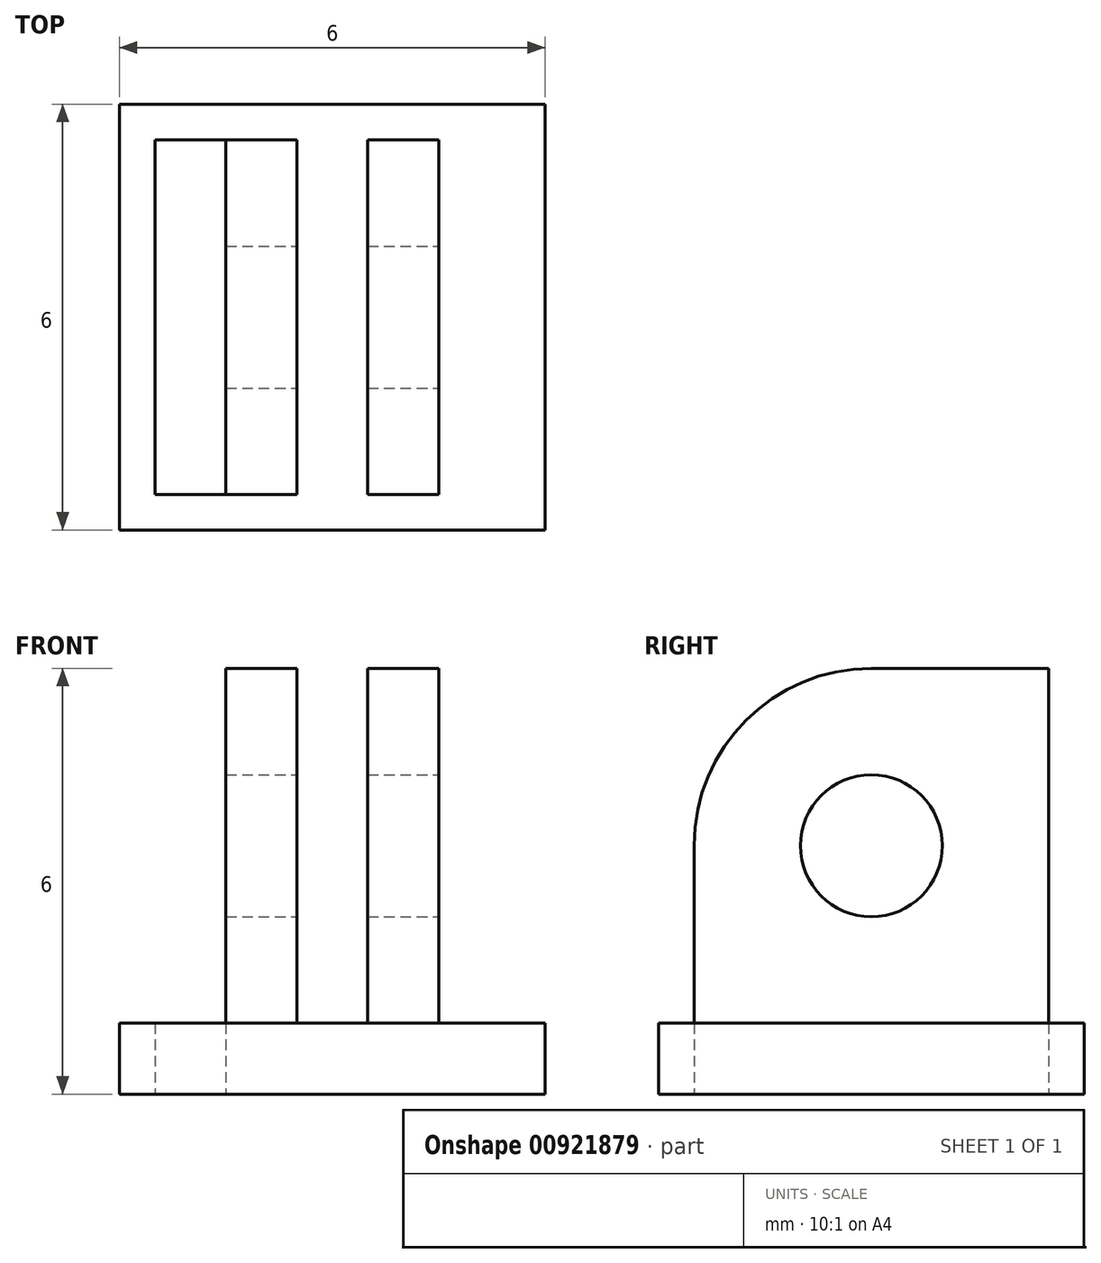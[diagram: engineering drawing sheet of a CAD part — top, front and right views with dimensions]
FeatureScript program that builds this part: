
annotation { "Feature Type Name" : "Feature", "Feature Type Description" : "" }
export const myFeature = defineFeature(function(context is Context, id is Id, definition is map)
    precondition{}
    {
        {
            var Q0;
            Q0=qCreatedBy(makeId("Top.planeOp"),FACE);
            var sketch = newSketch(context, id + "F0", { "sketchPlane" : qUnion([Q0])});
            skLineSegment(sketch, "E0.bottom", {"start": v(3, -3) * mm, "end": v(-3, -3) * mm});
            skLineSegment(sketch, "E0.top", {"start": v(3, 3) * mm, "end": v(-3, 3) * mm});
            skLineSegment(sketch, "E0.left", {"start": v(3, -3) * mm, "end": v(3, 3) * mm});
            skLineSegment(sketch, "E0.right", {"start": v(-3, -3) * mm, "end": v(-3, 3) * mm});
            skPoint(sketch, "E0.middle", {"position": v(0, 0) * mm});
            skLineSegment(sketch, "E1.bottom", {"start": v(2.5, -2.5) * mm, "end": v(1.5, -2.5) * mm});
            skLineSegment(sketch, "E1.top", {"start": v(1.5, 2.5) * mm, "end": v(0.5, 2.5) * mm});
            skLineSegment(sketch, "E1.left", {"start": v(2.5, -2.5) * mm, "end": v(2.5, 2.5) * mm});
            skLineSegment(sketch, "E1.right", {"start": v(-2.5, -2.5) * mm, "end": v(-2.5, 2.5) * mm});
            skLineSegment(sketch, "E2.bottom", {"start": v(-2.5, 2.5) * mm, "end": v(-1.5, 2.5) * mm});
            skLineSegment(sketch, "E2.top", {"start": v(-2.5, -2.5) * mm, "end": v(-1.5, -2.5) * mm});
            skLineSegment(sketch, "E2.left", {"start": v(-2.5, 2.5) * mm, "end": v(-2.5, -2.5) * mm});
            skLineSegment(sketch, "E2.right", {"start": v(-1.5, 2.5) * mm, "end": v(-1.5, -2.5) * mm});
            skLineSegment(sketch, "E3.bottom", {"start": v(-1.5, 2.5) * mm, "end": v(-0.5, 2.5) * mm});
            skLineSegment(sketch, "E3.right", {"start": v(-0.5, 2.5) * mm, "end": v(-0.5, -2.5) * mm});
            skLineSegment(sketch, "E4.top", {"start": v(-0.5, -2.5) * mm, "end": v(0.5, -2.5) * mm});
            skLineSegment(sketch, "E4.right", {"start": v(0.5, 2.5) * mm, "end": v(0.5, -2.5) * mm});
            skLineSegment(sketch, "E5.trimOffspring", {"start": v(-1.5, -2.5) * mm, "end": v(-2.5, -2.5) * mm});
            skLineSegment(sketch, "E6", {"start": v(-1.5, -2.5) * mm, "end": v(-0.5, -2.5) * mm});
            skLineSegment(sketch, "E7.bottom", {"start": v(0.5, 2.5) * mm, "end": v(1.5, 2.5) * mm});
            skLineSegment(sketch, "E7.right", {"start": v(1.5, 2.5) * mm, "end": v(1.5, -2.5) * mm});
            skLineSegment(sketch, "E8.trimOffspring", {"start": v(-0.5, 2.5) * mm, "end": v(-2.5, 2.5) * mm});
            skLineSegment(sketch, "E9", {"start": v(-0.5, 2.5) * mm, "end": v(2.5, 2.5) * mm});
            skLineSegment(sketch, "E10.trimOffspring", {"start": v(0.5, -2.5) * mm, "end": v(-0.5, -2.5) * mm});
            skLineSegment(sketch, "E11", {"start": v(0.5, -2.5) * mm, "end": v(1.5, -2.5) * mm});
            skSolve(sketch);
        }
        {
            var Q0;
            Q0=makeQuery(id+"F0.imprint","IMPRINT",FACE,{"disambiguationData":[TD([[makeQuery(id+"F0.imprint","IMPRINT",EDGE,{"derivedFrom":sQuery(id+"F0.wireOp",EDGE,"E0.bottom")}),-1.0]])]});
            var Q1;
            Q1=makeQuery(id+"F0.imprint","IMPRINT",FACE,{"disambiguationData":[TD([[makeQuery(id+"F0.imprint","IMPRINT",EDGE,{"derivedFrom":sQuery(id+"F0.wireOp",EDGE,"E1.bottom")}),-1.0]])]});
            var Q2;
            {var subQ0=sQuery(id+"F0.wireOp",EDGE,"E4.right");Q2=makeQuery(id+"F0.imprint","IMPRINT",FACE,{"disambiguationData":[TD([[makeQuery(id+"F0.imprint","IMPRINT",EDGE,{"derivedFrom":subQ0}),1.0]])]});}
            var Q3;
            {var subQ0=sQuery(id+"F0.wireOp",EDGE,"E3.right");Q3=makeQuery(id+"F0.imprint","IMPRINT",FACE,{"disambiguationData":[TD([[makeQuery(id+"F0.imprint","IMPRINT",EDGE,{"derivedFrom":subQ0}),1.0]])]});}
            var Q4;
            {var subQ0=sQuery(id+"F0.wireOp",EDGE,"E2.right");Q4=makeQuery(id+"F0.imprint","IMPRINT",FACE,{"disambiguationData":[TD([[makeQuery(id+"F0.imprint","IMPRINT",EDGE,{"derivedFrom":subQ0}),1.0]])]});}
            var Q5;
            {var subQ0=sQuery(id+"F0.wireOp",EDGE,"E2.left");Q5=makeQuery(id+"F0.imprint","IMPRINT",FACE,{"disambiguationData":[TD([[makeQuery(id+"F0.imprint","IMPRINT",EDGE,{"derivedFrom":subQ0}),1.0]])]});}
            extrude(context, id + "F1", {"entities" : qUnion([Q0, Q1, Q2, Q3, Q4, Q5]), "depth" : 1 * mm, "offsetDistance" : 25 * mm});
        }
        {
            var Q0;
            {var subQ0=sQuery(id+"F0.wireOp",EDGE,"E4.right");Q0=makeQuery(id+"F0.imprint","IMPRINT",FACE,{"disambiguationData":[TD([[makeQuery(id+"F0.imprint","IMPRINT",EDGE,{"derivedFrom":subQ0}),1.0]])]});}
            var Q1;
            {var subQ0=sQuery(id+"F0.wireOp",EDGE,"E2.right");Q1=makeQuery(id+"F0.imprint","IMPRINT",FACE,{"disambiguationData":[TD([[makeQuery(id+"F0.imprint","IMPRINT",EDGE,{"derivedFrom":subQ0}),1.0]])]});}
            extrude(context, id + "F2", {"entities" : qUnion([Q0, Q1]), "operationType" : NewBodyOperationType.ADD, "depth" : 6 * mm, "offsetDistance" : 25 * mm});
        }
        {
            var Q0;
            Q0=makeQuery(id+"F2.opExtrude","CAP_EDGE",EDGE,{"disambiguationData":[OSD([sQuery(id+"F0.wireOp",EDGE,"E6")])],"isStart":false});
            var Q1;
            Q1=makeQuery(id+"F2.opExtrude","CAP_EDGE",EDGE,{"disambiguationData":[OSD([sQuery(id+"F0.wireOp",EDGE,"E11")])],"isStart":false});
            var Q2;
            Q2=makeQuery(id+"F2.opExtrude","CAP_EDGE",EDGE,{"disambiguationData":[OSD([sQuery(id+"F0.wireOp",EDGE,"E8.trimOffspring")])],"isStart":false});
            var Q3;
            Q3=makeQuery(id+"F2.opExtrude","CAP_EDGE",EDGE,{"disambiguationData":[OSD([sQuery(id+"F0.wireOp",EDGE,"E9")])],"isStart":false});
            fillet(context, id + "F3", {"entities" : qUnion([Q0, Q1, Q2, Q3]), "radius" : 2.5 * mm, "tangentPropagation" : true, "allowEdgeOverflow" : false});
        }
        {
            var Q0;
            Q0=makeQuery(id+"F2.opExtrude","SWEPT_FACE",FACE,{"disambiguationData":[OSD([sQuery(id+"F0.wireOp",EDGE,"E7.right")])]});
            var sketch = newSketch(context, id + "F4", { "sketchPlane" : qUnion([Q0])});
            skCircle(sketch, "E12", {"center": v(0, 3.5) * mm, "radius": 1 * mm});
            skSolve(sketch);
        }
        {
            var Q0;
            Q0=makeQuery(id+"F4.imprint","IMPRINT",FACE,{"disambiguationData":[TD([[makeQuery(id+"F4.imprint","IMPRINT",EDGE,{"derivedFrom":sQuery(id+"F4.wireOp",EDGE,"E12")}),1.0]])]});
            extrude(context, id + "F5", {"entities" : qUnion([Q0]), "operationType" : NewBodyOperationType.REMOVE, "oppositeDirection" : true, "depth" : 25 * mm, "offsetDistance" : 25 * mm});
        }
    });
